# Revit family: WIR-PHOTOCELL
name_source: partatom
category: Communication Devices
revit_build: Autodesk Revit 2014 (Build: 20130308_1515(x64)
units: mm (PartAtom-declared; Revit-internal decimal feet)

## types (1)
- WIR-PHOTOCELL
    Assembly Code = D5090
    Base = Metal-Hubbell-Galvanized_Steel
    Certifications = ETL/UL 916 Listed
Title 24 Listed
RoHS compliant
    Default Elevation = 48 "
    Description = The wiSCAPE® Photocell provides On/Off lighting control based on detected light. Designed for outdoor lighting applications that require an external photocell, the wiSCAPE Photocell is a bi-directional wireless RF device that can transmit daytime and nighttime commands to a group or zone of wiSCAPE-enabled luminaires
    Housing Material = Paint - Hubbell - Carbon Black
    Manufacturer = Hubbell Control Solutions
    Model = WIR-PHOTOCELL Series
    Product Documentation Link = https://hubbellcdn.com
    Product Features = • On/Off photocell
• Pre-programmed for out-of-the-box photocell operation
• On/Off lighting circuit control with 0-10V full-range dimming
• Bidirectional wirless RF Mesh communications
• Digital input available for motion sensor or switch control
• Military grade AES-128 communication encryption
• Multi-level grouping and multiple scenarios
• Adjustable minimum and maximum dimming levels
• Commercial-grade metering
• Complete integration with wiSCAPE software
    Product Page URL = https://www.hubbell.com
    Type Comments = wiSCAPE® External Fixture Module
    URL = https://www.hubbell.com
    Warranty = 5-Years Warranty

## geometry (parser evidence)
native form markers: Sweep x1
no freeform markers — native parametric forms only
